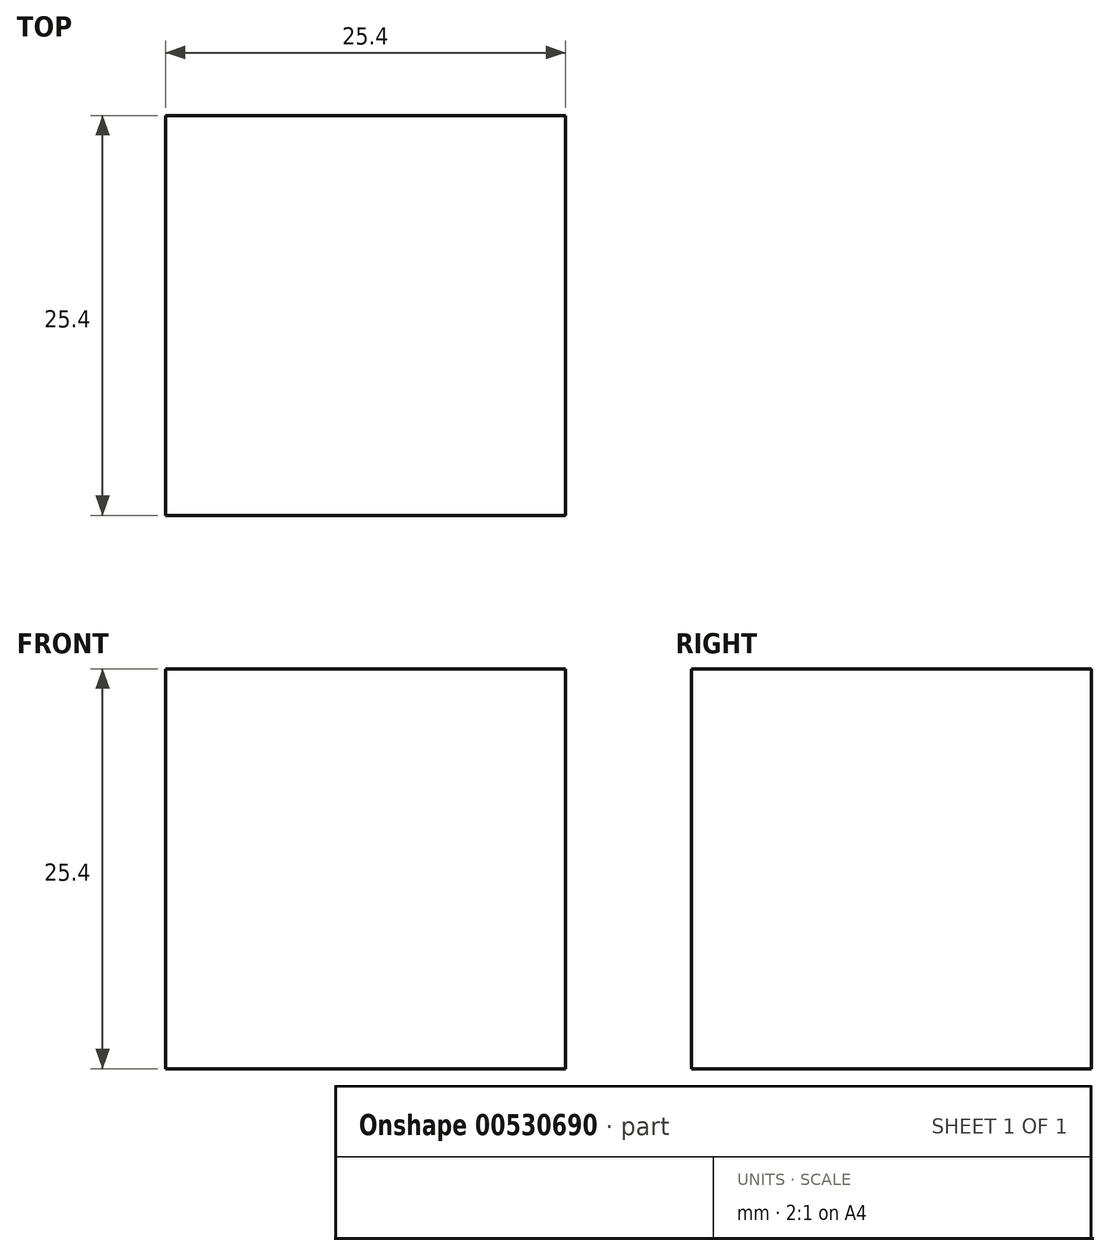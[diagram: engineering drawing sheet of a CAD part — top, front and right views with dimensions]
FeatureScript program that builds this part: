
annotation { "Feature Type Name" : "Feature", "Feature Type Description" : "" }
export const myFeature = defineFeature(function(context is Context, id is Id, definition is map)
    precondition{}
    {
        {
            var Q0;
            Q0=qCreatedBy(makeId("Top.planeOp"),FACE);
            var sketch = newSketch(context, id + "F0", { "sketchPlane" : qUnion([Q0])});
            skLineSegment(sketch, "E0.bottom", {"start": v(0, 0) * mm, "end": v(25.4, 0) * mm});
            skLineSegment(sketch, "E0.top", {"start": v(0, 25.4) * mm, "end": v(25.4, 25.4) * mm});
            skLineSegment(sketch, "E0.left", {"start": v(0, 0) * mm, "end": v(0, 25.4) * mm});
            skLineSegment(sketch, "E0.right", {"start": v(25.4, 0) * mm, "end": v(25.4, 25.4) * mm});
            skSolve(sketch);
        }
        {
            var Q0;
            Q0=qSketchRegion(id+"F0",true);
            extrude(context, id + "F1", {"entities" : qUnion([Q0]), "depth" : 25.4 * mm, "offsetDistance" : 25.4 * mm});
        }
    });
